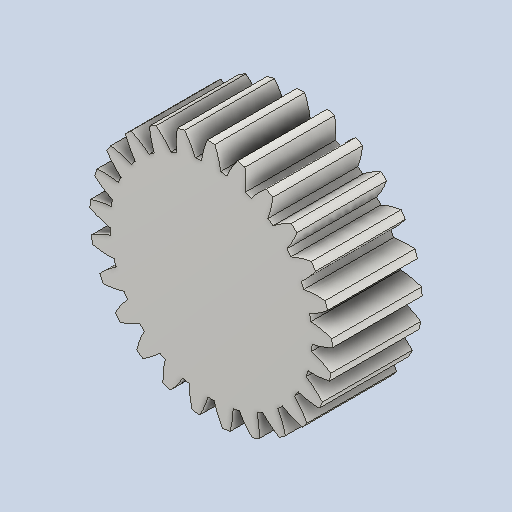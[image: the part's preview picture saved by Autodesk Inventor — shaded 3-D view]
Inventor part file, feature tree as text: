
AUTODESK INVENTOR PART (.ipt)
format: ipt  version: 2024 (Build 280153000, 153)  size: 267,776 bytes
history: native  units: mm (DEFAULTED — no unit token found)
features: plane x3, other x3, extrude x1, sketch x1
ambient origin geometry x8: Origin, YZ Plane, XZ Plane, XY Plane, X Axis, Y Axis, Z Axis, Center Point
bodies: Solid1 (feature_tree)
feature tree (8):
  extrude  "Extrusion1"  Depth=20.0mm TaperAngle=0.0deg
  plane  "Work Plane2"
  plane  "Work Plane8"
  plane  "Work Plane9"
  other  "Spur Gear"
  sketch  "Sketch1"  dims[d0=54.0mm d1=20.0mm d2=0.0mm d3=50.0mm d4=10.0mm d5=0.0mm d16=35.0mm d17=0.0mm d34=1.256637mm d39=0.0mm d41=0.0mm d43=35.0mm d46=35.0mm d47=0.0mm d48=0.0mm]
  other  "Srf1"
  other  "Pitch Diameter"
